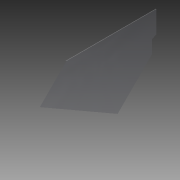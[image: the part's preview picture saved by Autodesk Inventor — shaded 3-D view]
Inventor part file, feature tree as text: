
AUTODESK INVENTOR PART (.ipt)
format: ipt  version: 2015 SP1 (Build 190203100, 203)  size: 120,832 bytes
history: native  units: in
note: dims shown in document units (in); Inventor stores cm internally (conversion verified against a paired STEP export)
features: sketch x2, extrude x1, hole x1, projected_geometry x1
ambient origin geometry x8: Origin, YZ Plane, XZ Plane, XY Plane, X Axis, Y Axis, Z Axis, Center Point
bodies: Solid1 (feature_tree)
feature tree (5):
  extrude  "Extrusion1"  TaperAngle=180.0deg  [1 undecoded]
  hole  "Hole1"  [1 undecoded]
  sketch  "Sketch1"  dims[d0=5.0in d1=180.0deg]
  sketch  "Sketch2"  dims[d8=7.922in d10=30.0in d11=90.0deg d13=90.0deg d14=90.0deg d16=0.125in d17=0.0in d18=112.5deg d19=3.125in d20=112.5deg d21=112.5deg d22=1.0in d23=0.0in d24=4.375in d25=1.75in d26=2.0in d27=0.5in d28=0.25in d29=0.75in d30=0.375in d31=0.25in d32=0.5635in d33=1.0in d34=0.8108in d35=4.0in d36=7.625in]
  projected_geometry  "Projected Loop1"
note: 2 required parameter values undecoded (feature->parameter linkage not recoverable at this tier; creation-order binding heuristic only, values carry confidence <= 0.55)
